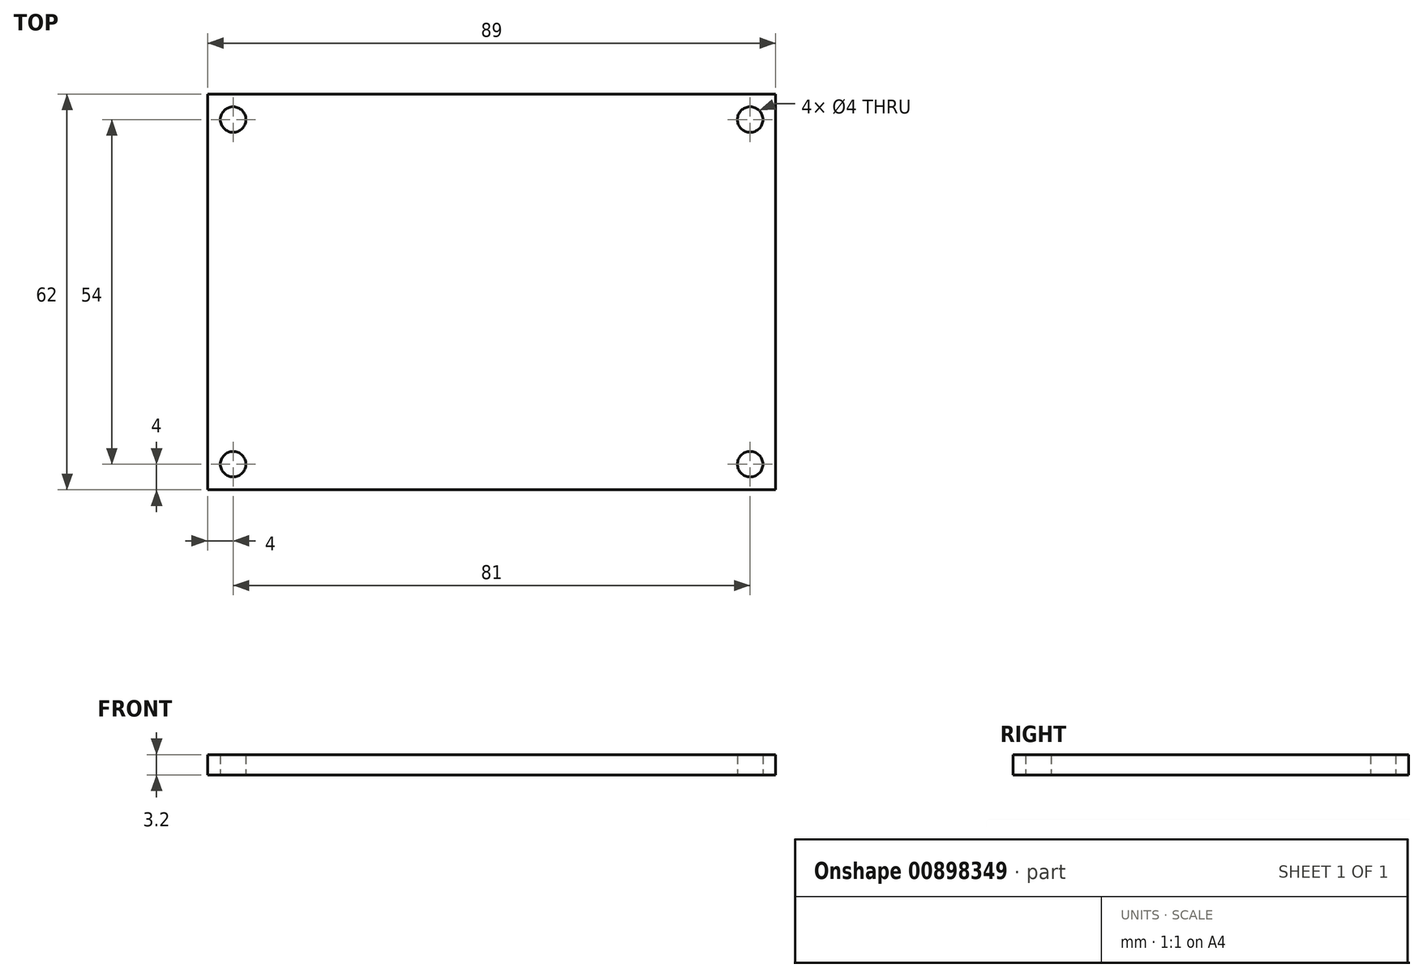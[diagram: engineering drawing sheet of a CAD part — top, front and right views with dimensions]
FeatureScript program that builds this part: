
annotation { "Feature Type Name" : "Feature", "Feature Type Description" : "" }
export const myFeature = defineFeature(function(context is Context, id is Id, definition is map)
    precondition{}
    {
        {
            var Q0;
            Q0=qCreatedBy(makeId("Top.planeOp"),FACE);
            var sketch = newSketch(context, id + "F0", { "sketchPlane" : qUnion([Q0])});
            skLineSegment(sketch, "E0.bottom", {"start": v(44.5, -31) * mm, "end": v(-44.5, -31) * mm});
            skLineSegment(sketch, "E0.top", {"start": v(44.5, 31) * mm, "end": v(-44.5, 31) * mm});
            skLineSegment(sketch, "E0.left", {"start": v(44.5, -31) * mm, "end": v(44.5, 31) * mm});
            skLineSegment(sketch, "E0.right", {"start": v(-44.5, -31) * mm, "end": v(-44.5, 31) * mm});
            skPoint(sketch, "E0.middle", {"position": v(0, 0) * mm});
            skCircle(sketch, "E1", {"center": v(-40.5, 27) * mm, "radius": 2 * mm});
            skCircle(sketch, "E2.MirrorC", {"center": v(40.5, 27) * mm, "radius": 2 * mm});
            skCircle(sketch, "E3.MirrorC", {"center": v(40.5, -27) * mm, "radius": 2 * mm});
            skCircle(sketch, "E4.MirrorC", {"center": v(-40.5, -27) * mm, "radius": 2 * mm});
            skSolve(sketch);
        }
        {
            var Q0;
            Q0=makeQuery(id+"F0.imprint","IMPRINT",FACE,{"disambiguationData":[TD([[makeQuery(id+"F0.imprint","IMPRINT",EDGE,{"derivedFrom":sQuery(id+"F0.wireOp",EDGE,"E0.bottom")}),-1.0]])]});
            extrude(context, id + "F1", {"entities" : qUnion([Q0]), "depth" : 3.2 * mm, "offsetDistance" : 25 * mm});
        }
    });
